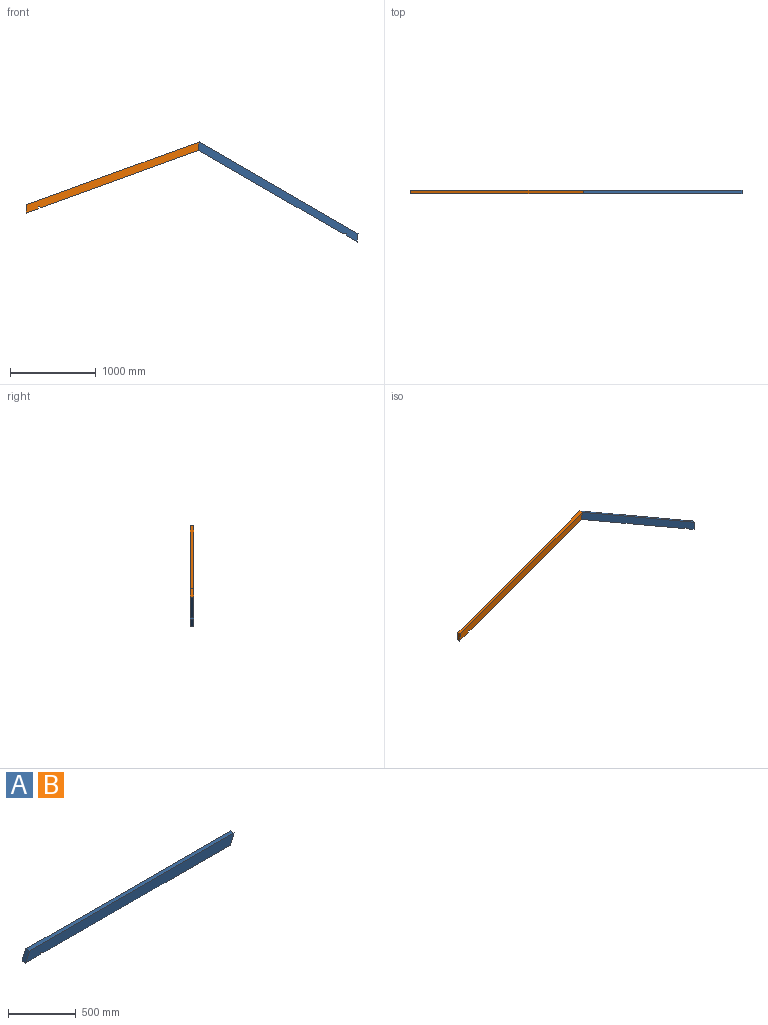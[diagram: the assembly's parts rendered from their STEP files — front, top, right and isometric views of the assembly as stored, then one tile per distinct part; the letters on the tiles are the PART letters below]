
ASSEMBLY  parts=2 mates=1
PART A: 9 faces, bbox 2181.4x38.1x88.9 mm
  f0: plane 88.9x41.45mm, normal (0.91,0,-0.42), area 3737.2mm2, adj f1,f6,f7,f8
  f1: plane 2139.95x38.1mm, normal (0,0,1), area 81532.1mm2, adj f0,f2,f7,f8
  f2: plane 88.9x41.45mm, normal (-0.91,0,0.42), area 3737.2mm2, adj f1,f3,f7,f8
  f3: plane 150.38x38.1mm, normal (0,0,-1), area 5729.4mm2, adj f2,f4,f7,f8
  f4: plane 38.1x19.05mm, normal (0.91,0,-0.4), area 793.4mm2, adj f3,f5,f7,f8
  f5: plane 43.14x38.1mm, normal (-0.4,0,-0.91), area 1796.7mm2, adj f4,f6,f7,f8
  f6: plane 1938.02x38.1mm, normal (0,0,-1), area 73838.6mm2, adj f0,f5,f7,f8
  f7: plane 2181.4x88.9mm, normal (0,-1,0), area 189750.5mm2, adj f0,f1,f2,f3,f4,f5,f6
  f8: plane 2181.4x88.9mm, normal (0,1,0), area 189750.5mm2, adj f0,f1,f2,f3,f4,f5,f6
PART B: same geometry as A
PLACE A rot(axis=(0.26,0,0.97),180deg) t=(952.42,-119.2,-461.84)mm
PLACE B rot(axis=(0,-1,0),20deg) t=(-979.65,-81.1,-292.81)mm
MATE fastened B.f0 <-> A.f0  axis (1,0,-0.09) through (25.8,-100.15,73.15)mm
